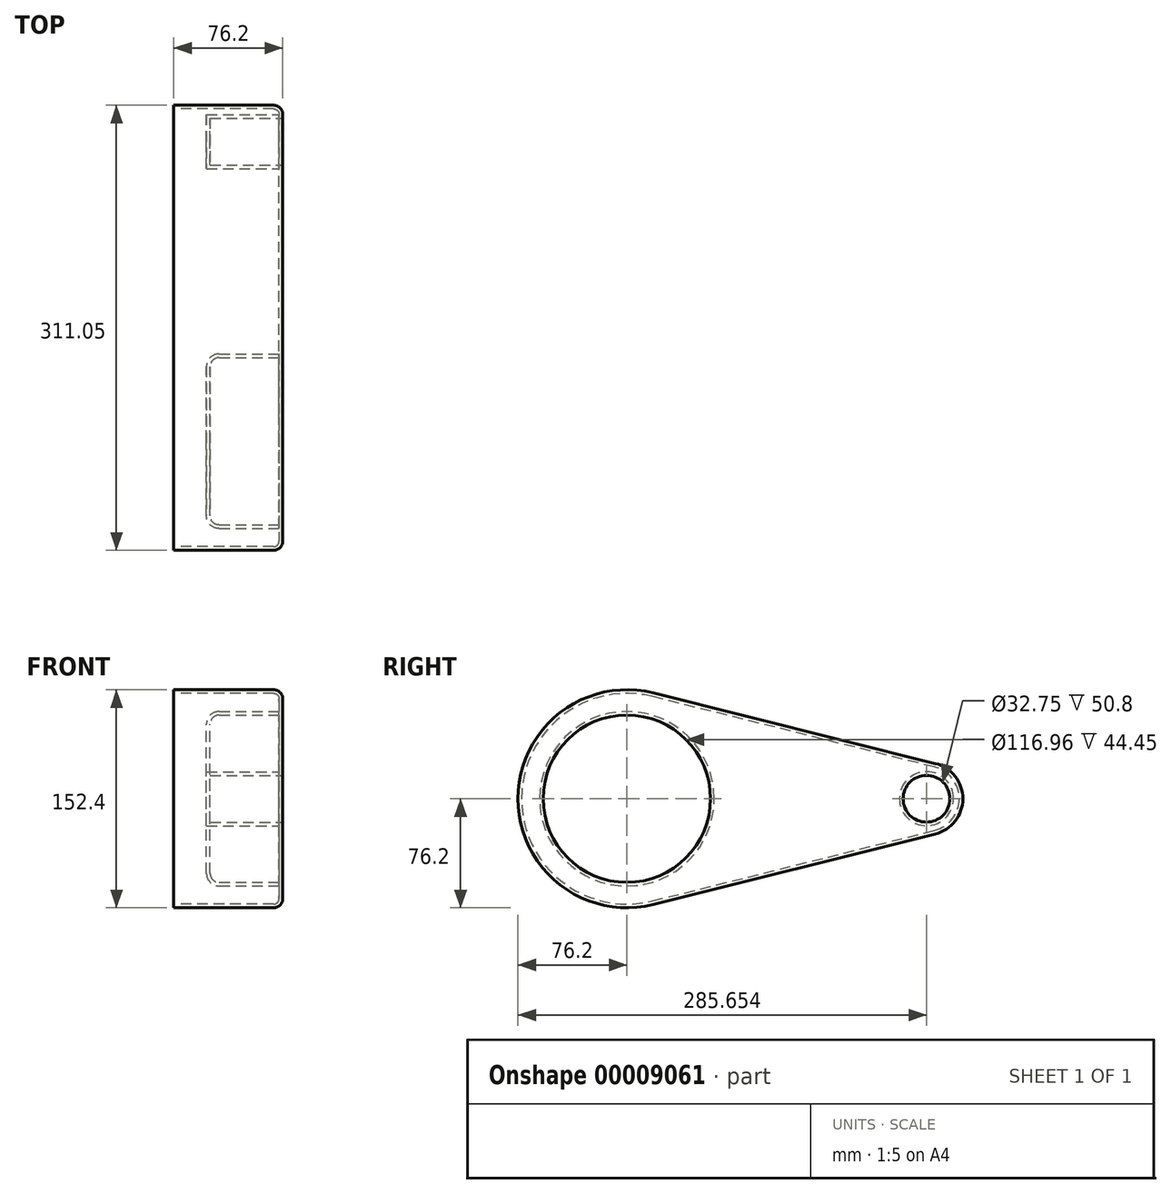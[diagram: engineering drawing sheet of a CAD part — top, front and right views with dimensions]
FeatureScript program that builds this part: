
annotation { "Feature Type Name" : "Feature", "Feature Type Description" : "" }
export const myFeature = defineFeature(function(context is Context, id is Id, definition is map)
    precondition{}
    {
        {
            var Q0;
            Q0=qCreatedBy(makeId("Right.planeOp"),FACE);
            var sketch = newSketch(context, id + "F0", { "sketchPlane" : qUnion([Q0])});
            skCircle(sketch, "E0", {"center": v(0, 0) * mm, "radius": 76.2 * mm});
            skCircle(sketch, "E1", {"center": v(209.45, 0) * mm, "radius": 25.4 * mm});
            skLineSegment(sketch, "E2", {"start": v(215.61, 24.64) * mm, "end": v(18.48, 73.92) * mm});
            skLineSegment(sketch, "E3", {"start": v(18.48, -73.92) * mm, "end": v(215.61, -24.64) * mm});
            skSolve(sketch);
        }
        {
            var Q0;
            {var subQ1=sQuery(id+"F0.wireOp",EDGE,"E2");Q0=makeQuery(id+"F0.imprint","IMPRINT",FACE,{"disambiguationData":[TD([[makeQuery(id+"F0.imprint","IMPRINT",EDGE,{"derivedFrom":subQ1}),1.0]])]});}
            var Q1;
            Q1 = qSketchRegion(id + "F0", true);
            extrude(context, id + "F1", {"entities" : qUnion([Q0, Q1]), "depth" : 76.2 * mm});
        }
        {
            var Q0;
            Q0=makeQuery(id+"F1.opExtrude","CAP_FACE",FACE,{"disambiguationData":[OSD([sQuery(id+"F0.wireOp",EDGE,"E0"),sQuery(id+"F0.wireOp",EDGE,"E1"),sQuery(id+"F0.wireOp",EDGE,"E2"),sQuery(id+"F0.wireOp",EDGE,"E3")])],"isStart":false});
            var sketch = newSketch(context, id + "F2", { "sketchPlane" : qUnion([Q0])});
            skCircle(sketch, "E4", {"center": v(0, 0) * mm, "radius": 58.48 * mm});
            skCircle(sketch, "E5", {"center": v(209.45, 0) * mm, "radius": 16.37 * mm});
            skSolve(sketch);
        }
        {
            var Q0;
            Q0 = qSketchRegion(id + "F2", true);
            extrude(context, id + "F3", {"entities" : qUnion([Q0]), "operationType" : NewBodyOperationType.REMOVE, "oppositeDirection" : true, "depth" : 50.8 * mm});
        }
        {
            var Q0;
            Q0=makeQuery(id+"F3.boolean.opBoolean","COPY",EDGE,{"derivedFrom":makeQuery(id+"F3.opExtrude","CAP_EDGE",EDGE,{"disambiguationData":[OSD([sQuery(id+"F2.wireOp",EDGE,"E4")])],"isStart":true})});
            var Q1;
            Q1=makeQuery(id+"F3.boolean.opBoolean","COPY",EDGE,{"derivedFrom":makeQuery(id+"F3.opExtrude","CAP_EDGE",EDGE,{"disambiguationData":[OSD([sQuery(id+"F2.wireOp",EDGE,"E5")])],"isStart":true})});
            var Q2;
            Q2=makeQuery(id+"F3.boolean.opBoolean","COPY",EDGE,{"derivedFrom":makeQuery(id+"F3.opExtrude","CAP_EDGE",EDGE,{"disambiguationData":[OSD([sQuery(id+"F2.wireOp",EDGE,"E4")])],"isStart":false})});
            var Q3;
            Q3=makeQuery(id+"F1.opExtrude","CAP_EDGE",EDGE,{"disambiguationData":[OSD([sQuery(id+"F0.wireOp",EDGE,"E3")])],"isStart":false});
            var Q4;
            Q4=makeQuery(id+"F1.opExtrude","CAP_EDGE",EDGE,{"disambiguationData":[OSD([sQuery(id+"F0.wireOp",EDGE,"E0")])],"isStart":false});
            var Q5;
            Q5=makeQuery(id+"F1.opExtrude","CAP_EDGE",EDGE,{"disambiguationData":[OSD([sQuery(id+"F0.wireOp",EDGE,"E2")])],"isStart":false});
            var Q6;
            Q6=makeQuery(id+"F1.opExtrude","CAP_EDGE",EDGE,{"disambiguationData":[OSD([sQuery(id+"F0.wireOp",EDGE,"E1")])],"isStart":false});
            fillet(context, id + "F4", {"entities" : qUnion([Q0, Q1, Q2, Q3, Q4, Q5, Q6]), "radius" : 6.35 * mm, "tangentPropagation" : true, "allowEdgeOverflow" : false});
        }
        {
            var Q0;
            Q0=makeQuery(id+"F1.opExtrude","CAP_FACE",FACE,{"disambiguationData":[OSD([sQuery(id+"F0.wireOp",EDGE,"E0"),sQuery(id+"F0.wireOp",EDGE,"E1"),sQuery(id+"F0.wireOp",EDGE,"E2"),sQuery(id+"F0.wireOp",EDGE,"E3")])],"isStart":true});
            shell(context, id + "F5", {"entities" : qUnion([Q0]), "thickness" : 2.54 * mm});
        }
    });
